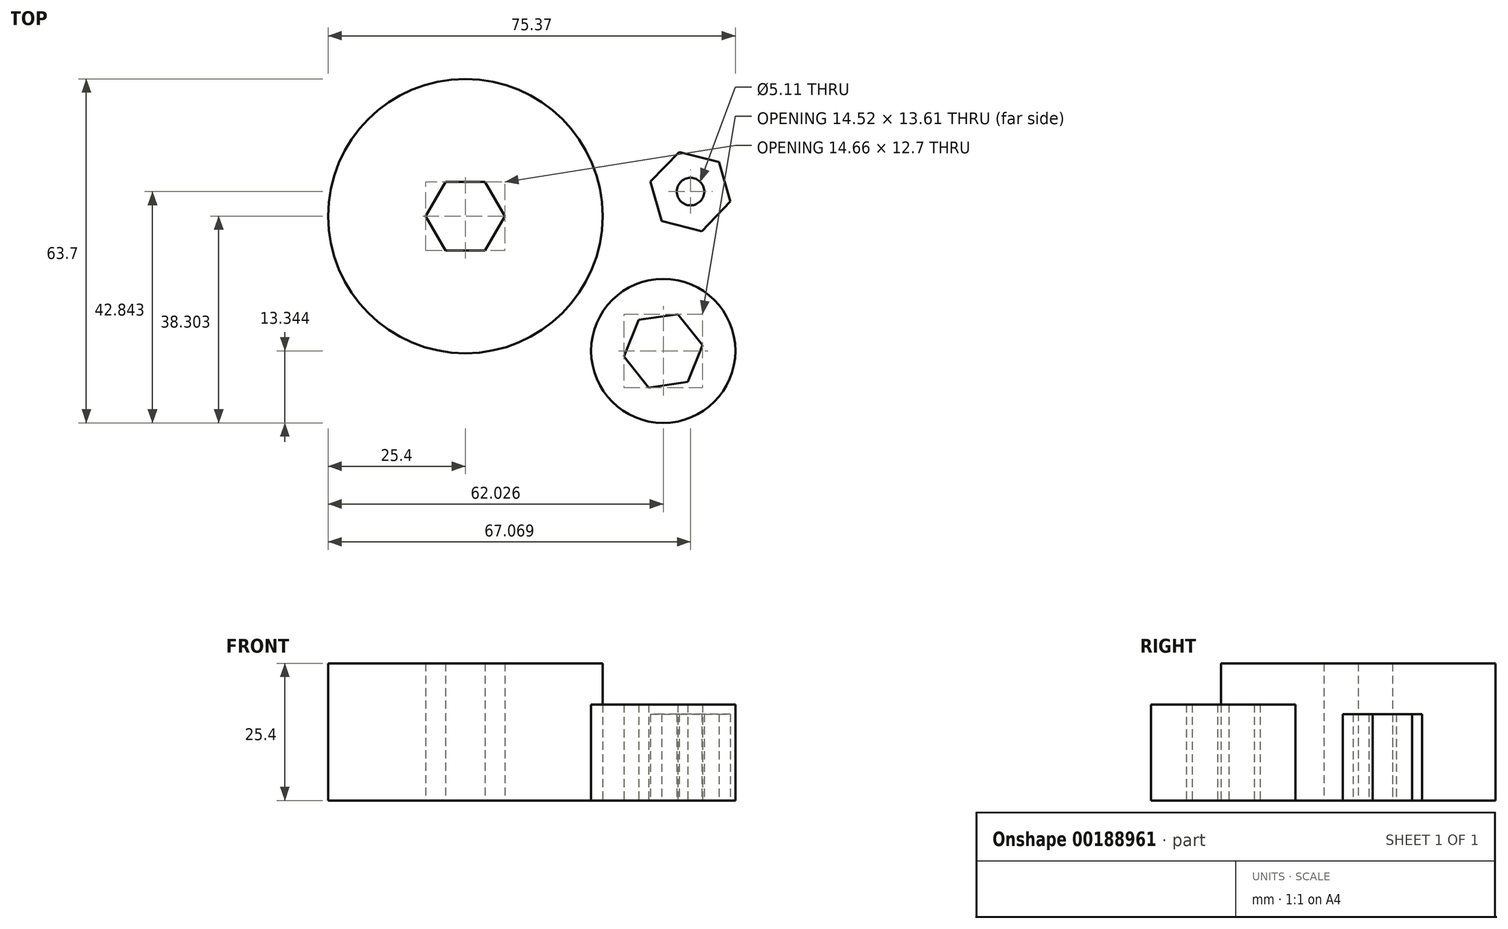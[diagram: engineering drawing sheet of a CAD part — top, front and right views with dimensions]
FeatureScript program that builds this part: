
annotation { "Feature Type Name" : "Feature", "Feature Type Description" : "" }
export const myFeature = defineFeature(function(context is Context, id is Id, definition is map)
    precondition{}
    {
        {
            assignVariable(context, id + "F0", {"name" : "width", "anyValue" : 16});
        }
        {
            assignVariable(context, id + "F1", {"name" : "wheel_width", "anyValue" : 25.4 * mm});
        }
        {
            var Q0;
            Q0=qCreatedBy(makeId("Top.planeOp"),FACE);
            var sketch = newSketch(context, id + "F2", { "sketchPlane" : qUnion([Q0])});
            skCircle(sketch, "E0", {"center": v(-80.67, 51.23) * mm, "radius": 25.4 * mm});
            skCircle(sketch, "E1.cCircle", {"center": v(-80.67, 51.23) * mm, "radius": 6.35 * mm, "construction": true});
            skLineSegment(sketch, "E1.0", {"start": v(-77, 44.88) * mm, "end": v(-84.34, 44.88) * mm});
            skLineSegment(sketch, "E1.1", {"start": v(-84.34, 44.88) * mm, "end": v(-88, 51.23) * mm});
            skLineSegment(sketch, "E1.2", {"start": v(-88, 51.23) * mm, "end": v(-84.34, 57.58) * mm});
            skLineSegment(sketch, "E1.3", {"start": v(-84.34, 57.58) * mm, "end": v(-77, 57.58) * mm});
            skLineSegment(sketch, "E1.4", {"start": v(-77, 57.58) * mm, "end": v(-73.34, 51.23) * mm});
            skLineSegment(sketch, "E1.5", {"start": v(-73.34, 51.23) * mm, "end": v(-77, 44.88) * mm});
            skPoint(sketch, "E1.0.midPoint", {"position": v(-80.67, 44.88) * mm});
            skSolve(sketch);
        }
        {
            var Q0;
            Q0=makeQuery(id+"F2.imprint","IMPRINT",FACE,{"disambiguationData":[TD([[makeQuery(id+"F2.imprint","IMPRINT",EDGE,{"derivedFrom":sQuery(id+"F2.wireOp",EDGE,"E0")}),1.0]])]});
            extrude(context, id + "F3", {"entities" : qUnion([Q0]), "depth" : getVariable(context, 'wheel_width')});
        }
        {
            var Q0;
            Q0=qCreatedBy(makeId("Top.planeOp"),FACE);
            var sketch = newSketch(context, id + "F4", { "sketchPlane" : qUnion([Q0])});
            skCircle(sketch, "E2.cCircle", {"center": v(-39, 55.77) * mm, "radius": 6.6 * mm, "construction": true});
            skLineSegment(sketch, "E2.0", {"start": v(-31.6, 53.92) * mm, "end": v(-36.9, 48.44) * mm});
            skLineSegment(sketch, "E2.1", {"start": v(-36.9, 48.44) * mm, "end": v(-44.3, 50.29) * mm});
            skLineSegment(sketch, "E2.2", {"start": v(-44.3, 50.29) * mm, "end": v(-46.4, 57.62) * mm});
            skLineSegment(sketch, "E2.3", {"start": v(-46.4, 57.62) * mm, "end": v(-41.1, 63.1) * mm});
            skLineSegment(sketch, "E2.4", {"start": v(-41.1, 63.1) * mm, "end": v(-33.7, 61.26) * mm});
            skLineSegment(sketch, "E2.5", {"start": v(-33.7, 61.26) * mm, "end": v(-31.6, 53.92) * mm});
            skPoint(sketch, "E2.0.midPoint", {"position": v(-34.25, 51.18) * mm});
            skCircle(sketch, "E3", {"center": v(-39, 55.77) * mm, "radius": 2.55 * mm});
            skSolve(sketch);
        }
        {
            var Q0;
            Q0 = qSketchRegion(id + "F4", true);
            extrude(context, id + "F5", {"entities" : qUnion([Q0]), "depth" : (getVariable(context, 'width')) * mm});
        }
        {
            var Q0;
            Q0=qCreatedBy(makeId("Top.planeOp"),FACE);
            var sketch = newSketch(context, id + "F6", { "sketchPlane" : qUnion([Q0])});
            skCircle(sketch, "E4", {"center": v(-44.04, 26.27) * mm, "radius": 13.34 * mm});
            skCircle(sketch, "E5.cCircle", {"center": v(-44.04, 26.27) * mm, "radius": 6.35 * mm, "construction": true});
            skLineSegment(sketch, "E5.0", {"start": v(-39.51, 20.5) * mm, "end": v(-46.77, 19.47) * mm});
            skLineSegment(sketch, "E5.1", {"start": v(-46.77, 19.47) * mm, "end": v(-51.3, 25.23) * mm});
            skLineSegment(sketch, "E5.2", {"start": v(-51.3, 25.23) * mm, "end": v(-48.57, 32.04) * mm});
            skLineSegment(sketch, "E5.3", {"start": v(-48.57, 32.04) * mm, "end": v(-41.32, 33.08) * mm});
            skLineSegment(sketch, "E5.4", {"start": v(-41.32, 33.08) * mm, "end": v(-36.79, 27.31) * mm});
            skLineSegment(sketch, "E5.5", {"start": v(-36.79, 27.31) * mm, "end": v(-39.51, 20.5) * mm});
            skPoint(sketch, "E5.0.midPoint", {"position": v(-43.14, 19.99) * mm});
            skSolve(sketch);
        }
        {
            var Q0;
            Q0 = qSketchRegion(id + "F6", true);
            extrude(context, id + "F7", {"entities" : qUnion([Q0]), "depth" : 17.78 * mm});
        }
    });
